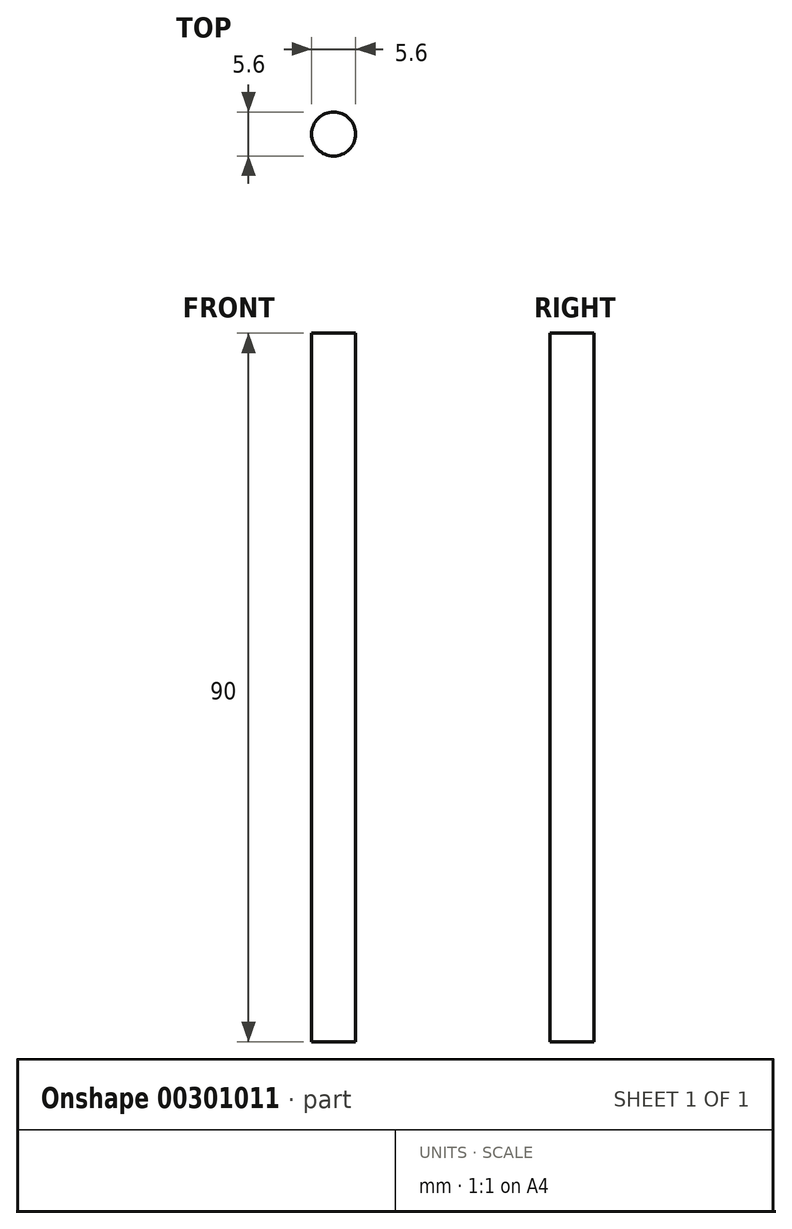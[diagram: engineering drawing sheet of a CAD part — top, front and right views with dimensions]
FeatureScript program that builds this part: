
annotation { "Feature Type Name" : "Feature", "Feature Type Description" : "" }
export const myFeature = defineFeature(function(context is Context, id is Id, definition is map)
    precondition{}
    {
        {
            var Q0;
            Q0=qCreatedBy(makeId("Top.planeOp"),FACE);
            var sketch = newSketch(context, id + "F0", { "sketchPlane" : qUnion([Q0])});
            skCircle(sketch, "E0", {"center": v(0, 0) * mm, "radius": 2.8 * mm});
            skSolve(sketch);
        }
        {
            var Q0;
            Q0=makeQuery(id+"F0.imprint","IMPRINT",FACE,{"disambiguationData":[TD([[makeQuery(id+"F0.imprint","IMPRINT",EDGE,{"derivedFrom":sQuery(id+"F0.wireOp",EDGE,"E0")}),1.0]])]});
            extrude(context, id + "F1", {"entities" : qUnion([Q0]), "depth" : 90 * mm, "offsetDistance" : 25 * mm});
        }
    });
